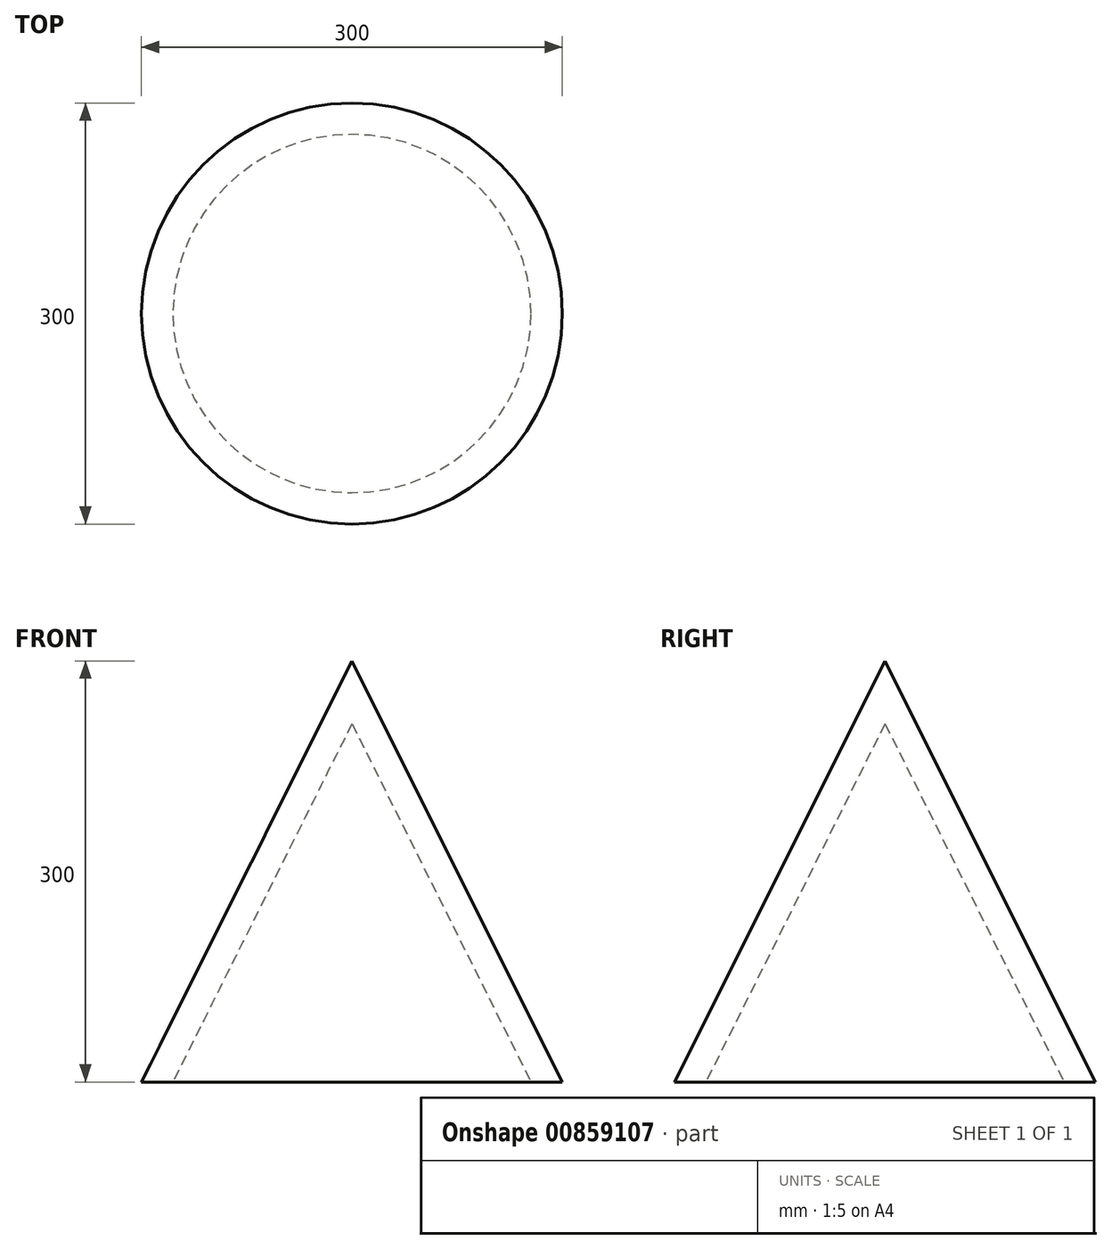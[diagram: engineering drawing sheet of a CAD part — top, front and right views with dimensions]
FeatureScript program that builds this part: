
annotation { "Feature Type Name" : "Feature", "Feature Type Description" : "" }
export const myFeature = defineFeature(function(context is Context, id is Id, definition is map)
    precondition{}
    {
        {
            var Q0;
            Q0=qCreatedBy(makeId("Front.planeOp"),FACE);
            var sketch = newSketch(context, id + "F0", { "sketchPlane" : qUnion([Q0])});
            skLineSegment(sketch, "E0", {"start": v(0, 0) * mm, "end": v(150, 0) * mm});
            skLineSegment(sketch, "E1", {"start": v(0, 0) * mm, "end": v(0, 300) * mm});
            skLineSegment(sketch, "E2", {"start": v(0, 300) * mm, "end": v(150, 0) * mm});
            skLineSegment(sketch, "E3", {"start": v(108.9, 37.5) * mm, "end": v(127.64, 0) * mm});
            skLineSegment(sketch, "E4", {"start": v(127.64, 0) * mm, "end": v(0, 255.28) * mm});
            skSolve(sketch);
        }
        {
            var Q0;
            {var subQ1=sQuery(id+"F0.wireOp",EDGE,"E2");Q0=makeQuery(id+"F0.imprint","IMPRINT",FACE,{"disambiguationData":[TD([[makeQuery(id+"F0.imprint","IMPRINT",EDGE,{"derivedFrom":subQ1}),-1.0]])]});}
            var Q1;
            Q1=sQuery(id+"F0.wireOp",EDGE,"E1");
            revolve(context, id + "F1", {"surfaceOperationType" : NewSurfaceOperationType.NEW, "entities" : qUnion([Q0]), "axis" : qUnion([Q1]), "revolveType" : RevolveType.FULL});
        }
    });
